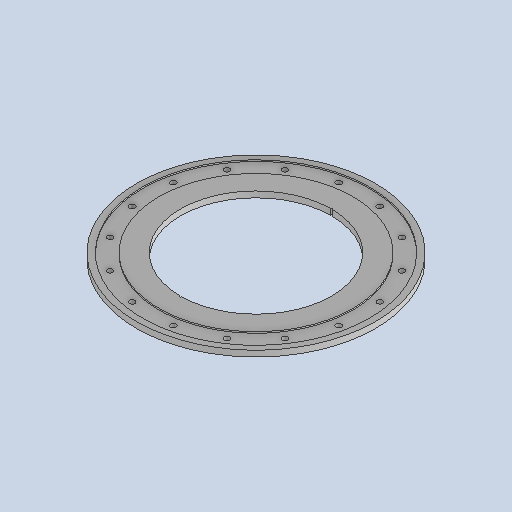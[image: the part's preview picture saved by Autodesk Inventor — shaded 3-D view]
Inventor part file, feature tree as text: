
AUTODESK INVENTOR PART (.ipt)
format: ipt  version: 2025 (Build 290162010, 162A)  size: 396,800 bytes
history: native  units: mm
features: extrude x4, sketch x4, pattern_circular x1, mirror x1, projected_geometry x1, other x1
ambient origin geometry x8: Origin, YZ Plane, XZ Plane, XY Plane, X Axis, Y Axis, Z Axis, Center Point
bodies: Solid1 (feature_tree)
feature tree (12):
  extrude  "Extrusion1"  Depth=15.0mm
  extrude  "Extrusion2"  TaperAngle=0.0deg  [1 undecoded]
  extrude  "Extrusion3"  Depth=530.0mm
  pattern_circular  "Circular Pattern2"  [2 undecoded]
  extrude  "Extrusion4"  Depth=160.0mm TaperAngle=360.0deg
  mirror  "Mirror1"
  sketch  "Sketch1"  dims[d2=15.0mm d3=0.0mm d4=42.0mm]
  sketch  "Sketch2"  dims[d6=3.5mm d7=0.0mm d10=0.0mm d11=0.0mm]
  projected_geometry  "Projected Loop1"
  sketch  "Sketch3"  dims[d17=530.0mm d19=530.0mm]
  sketch  "Sketch5"  dims[d20=1.963495mm d21=14.0mm d22=160.0mm d23=360.0deg d34=0.0mm d35=0.0mm d40=6.0mm d41=602.0mm d42=380.0mm]
  other  "Definition1"
note: 3 required parameter values undecoded (feature->parameter linkage not recoverable at this tier; creation-order binding heuristic only, values carry confidence <= 0.55)
